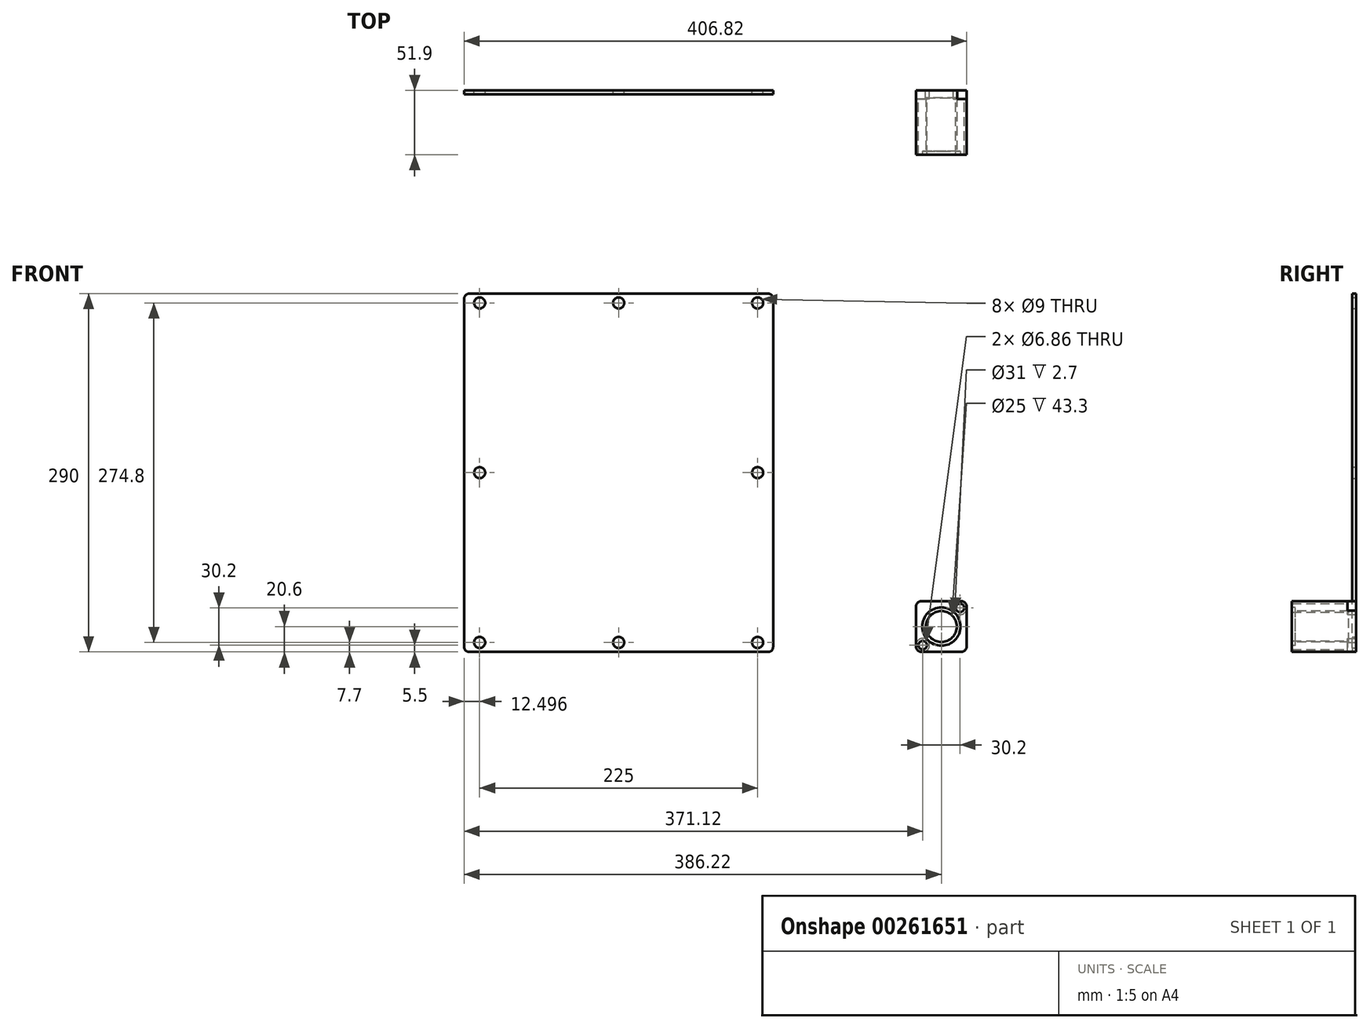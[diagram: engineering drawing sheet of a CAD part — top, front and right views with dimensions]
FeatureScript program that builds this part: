
annotation { "Feature Type Name" : "Feature", "Feature Type Description" : "" }
export const myFeature = defineFeature(function(context is Context, id is Id, definition is map)
    precondition{}
    {
        {
            var Q0;
            Q0=qCreatedBy(makeId("Front.planeOp"),FACE);
            var sketch = newSketch(context, id + "F0", { "sketchPlane" : qUnion([Q0])});
            skLineSegment(sketch, "E0.bottom", {"start": v(0, 0) * mm, "end": v(41.2, 0) * mm});
            skLineSegment(sketch, "E0.top", {"start": v(0, 41.2) * mm, "end": v(41.2, 41.2) * mm});
            skLineSegment(sketch, "E0.left", {"start": v(0, 0) * mm, "end": v(0, 41.2) * mm});
            skLineSegment(sketch, "E0.right", {"start": v(41.2, 0) * mm, "end": v(41.2, 41.2) * mm});
            skCircle(sketch, "E1", {"center": v(5.5, 5.5) * mm, "radius": 3.43 * mm});
            skCircle(sketch, "E2", {"center": v(35.7, 35.7) * mm, "radius": 3.43 * mm});
            skCircle(sketch, "E3", {"center": v(35.7, 35.7) * mm, "radius": 5.5 * mm});
            skCircle(sketch, "E4", {"center": v(5.5, 5.5) * mm, "radius": 5.5 * mm});
            skSolve(sketch);
        }
        {
            var Q0;
            {var subQ0=sQuery(id+"F0.wireOp",EDGE,"E0.left");var subQ1=sQuery(id+"F0.wireOp",EDGE,"E0.bottom");var subQ2=makeQuery(id+"F0.imprint","INTERSECT",VERTEX,{"derivedFrom":[subQ1,subQ0]});Q0=makeQuery(id+"F0.imprint","IMPRINT",FACE,{"disambiguationData":[TD([[makeQuery(id+"F0.imprint","IMPRINT",EDGE,{"disambiguationData":[TD([[subQ2,-1.0]])],"derivedFrom":subQ1}),1.0]])]});}
            var Q1;
            {var subQ0=sQuery(id+"F0.wireOp",EDGE,"E0.right");var subQ1=sQuery(id+"F0.wireOp",EDGE,"E0.top");var subQ2=makeQuery(id+"F0.imprint","INTERSECT",VERTEX,{"derivedFrom":[subQ1,subQ0]});Q1=makeQuery(id+"F0.imprint","IMPRINT",FACE,{"disambiguationData":[TD([[makeQuery(id+"F0.imprint","IMPRINT",EDGE,{"disambiguationData":[TD([[subQ2,1.0]])],"derivedFrom":subQ1}),-1.0]])]});}
            var Q2;
            Q2=makeQuery(id+"F0.imprint","IMPRINT",FACE,{"disambiguationData":[TD([[makeQuery(id+"F0.imprint","IMPRINT",EDGE,{"derivedFrom":sQuery(id+"F0.wireOp",EDGE,"E1")}),-1.0]])]});
            var Q3;
            Q3=makeQuery(id+"F0.imprint","IMPRINT",FACE,{"disambiguationData":[TD([[makeQuery(id+"F0.imprint","IMPRINT",EDGE,{"derivedFrom":sQuery(id+"F0.wireOp",EDGE,"E2")}),-1.0]])]});
            var Q4;
            {var subQ0=sQuery(id+"F0.wireOp",EDGE,"E0.right");var subQ1=sQuery(id+"F0.wireOp",EDGE,"E0.bottom");var subQ2=makeQuery(id+"F0.imprint","INTERSECT",VERTEX,{"derivedFrom":[subQ1,subQ0]});Q4=makeQuery(id+"F0.imprint","IMPRINT",FACE,{"disambiguationData":[TD([[makeQuery(id+"F0.imprint","IMPRINT",EDGE,{"disambiguationData":[TD([[subQ2,1.0]])],"derivedFrom":subQ1}),1.0]])]});}
            extrude(context, id + "F1", {"entities" : qUnion([Q0, Q1, Q2, Q3, Q4]), "depth" : 51.9 * mm});
        }
        {
            var Q0;
            Q0=makeQuery(id+"F1.opExtrude","CAP_FACE",FACE,{"disambiguationData":[OSD([sQuery(id+"F0.wireOp",EDGE,"E0.bottom"),sQuery(id+"F0.wireOp",EDGE,"E0.top"),sQuery(id+"F0.wireOp",EDGE,"E0.left"),sQuery(id+"F0.wireOp",EDGE,"E0.right"),sQuery(id+"F0.wireOp",EDGE,"E1"),sQuery(id+"F0.wireOp",EDGE,"E2")])],"isStart":true});
            var sketch = newSketch(context, id + "F2", { "sketchPlane" : qUnion([Q0])});
            skCircle(sketch, "E5", {"center": v(-35.7, 35.7) * mm, "radius": 5.5 * mm});
            skCircle(sketch, "E6", {"center": v(-5.5, 5.5) * mm, "radius": 5.5 * mm});
            skLineSegment(sketch, "E7", {"start": v(7.84, 0) * mm, "end": v(0, -7.71) * mm});
            skLineSegment(sketch, "E8", {"start": v(-39.53, 31.76) * mm, "end": v(-49.04, 41) * mm});
            skLineSegment(sketch, "E9", {"start": v(-49.04, 41) * mm, "end": v(-41.2, 48.71) * mm});
            skLineSegment(sketch, "E10", {"start": v(-41.2, 48.71) * mm, "end": v(-31.87, 39.64) * mm});
            skLineSegment(sketch, "E11", {"start": v(7.84, 0) * mm, "end": v(-1.62, 9.4) * mm});
            skLineSegment(sketch, "E12", {"start": v(0, -7.71) * mm, "end": v(-9.38, 1.6) * mm});
            skSolve(sketch);
        }
        {
            var Q0;
            Q0=makeQuery(id+"F2.imprint","IMPRINT",FACE,{"disambiguationData":[TD([[makeQuery(id+"F2.imprint","IMPRINT",EDGE,{"derivedFrom":makeQuery(id+"F1.opExtrude","CAP_EDGE",EDGE,{"disambiguationData":[OSD([sQuery(id+"F0.wireOp",EDGE,"E1")])],"isStart":true})}),1.0]])]});
            var Q1;
            {var subQ0=sQuery(id+"F2.wireOp",EDGE,"E5");var subQ1=makeQuery(id+"F1.opExtrude","CAP_EDGE",EDGE,{"disambiguationData":[OSD([sQuery(id+"F0.wireOp",EDGE,"E0.top")])],"isStart":true});var subQ2=makeQuery(id+"F2.imprint","INTERSECT",VERTEX,{"derivedFrom":[subQ1,subQ0]});Q1=makeQuery(id+"F2.imprint","IMPRINT",FACE,{"disambiguationData":[TD([[makeQuery(id+"F2.imprint","IMPRINT",EDGE,{"disambiguationData":[TD([[subQ2,-1.0]])],"derivedFrom":subQ0}),-1.0]])]});}
            var Q2;
            Q2=makeQuery(id+"F2.imprint","IMPRINT",FACE,{"disambiguationData":[TD([[makeQuery(id+"F2.imprint","IMPRINT",EDGE,{"derivedFrom":makeQuery(id+"F1.opExtrude","CAP_EDGE",EDGE,{"disambiguationData":[OSD([sQuery(id+"F0.wireOp",EDGE,"E2")])],"isStart":true})}),1.0]])]});
            var Q3;
            {var subQ0=sQuery(id+"F2.wireOp",EDGE,"E6");var subQ1=makeQuery(id+"F1.opExtrude","CAP_EDGE",EDGE,{"disambiguationData":[OSD([sQuery(id+"F0.wireOp",EDGE,"E0.left")])],"isStart":true});var subQ2=makeQuery(id+"F2.imprint","INTERSECT",VERTEX,{"derivedFrom":[subQ1,subQ0]});Q3=makeQuery(id+"F2.imprint","IMPRINT",FACE,{"disambiguationData":[TD([[makeQuery(id+"F2.imprint","IMPRINT",EDGE,{"disambiguationData":[TD([[subQ2,1.0]])],"derivedFrom":subQ0}),-1.0]])]});}
            var Q4;
            {var subQ0=sQuery(id+"F2.wireOp",EDGE,"E11");var subQ1=sQuery(id+"F2.wireOp",EDGE,"E6");var subQ2=makeQuery(id+"F2.imprint","INTERSECT",VERTEX,{"derivedFrom":[subQ1,subQ0]});Q4=makeQuery(id+"F2.imprint","IMPRINT",FACE,{"disambiguationData":[TD([[makeQuery(id+"F2.imprint","IMPRINT",EDGE,{"disambiguationData":[TD([[subQ2,1.0]])],"derivedFrom":subQ1}),-1.0]])]});}
            var Q5;
            {var subQ0=sQuery(id+"F2.wireOp",EDGE,"E12");var subQ1=sQuery(id+"F2.wireOp",EDGE,"E6");var subQ2=makeQuery(id+"F2.imprint","INTERSECT",VERTEX,{"derivedFrom":[subQ1,subQ0]});Q5=makeQuery(id+"F2.imprint","IMPRINT",FACE,{"disambiguationData":[TD([[makeQuery(id+"F2.imprint","IMPRINT",EDGE,{"disambiguationData":[TD([[subQ2,-1.0]])],"derivedFrom":subQ1}),-1.0]])]});}
            var Q6;
            {var subQ0=sQuery(id+"F2.wireOp",EDGE,"E10");var subQ1=sQuery(id+"F2.wireOp",EDGE,"E5");var subQ2=makeQuery(id+"F2.imprint","INTERSECT",VERTEX,{"derivedFrom":[subQ1,subQ0]});Q6=makeQuery(id+"F2.imprint","IMPRINT",FACE,{"disambiguationData":[TD([[makeQuery(id+"F2.imprint","IMPRINT",EDGE,{"disambiguationData":[TD([[subQ2,-1.0]])],"derivedFrom":subQ1}),-1.0]])]});}
            var Q7;
            {var subQ0=sQuery(id+"F2.wireOp",EDGE,"E8");var subQ1=sQuery(id+"F2.wireOp",EDGE,"E5");var subQ2=makeQuery(id+"F2.imprint","INTERSECT",VERTEX,{"derivedFrom":[subQ1,subQ0]});Q7=makeQuery(id+"F2.imprint","IMPRINT",FACE,{"disambiguationData":[TD([[makeQuery(id+"F2.imprint","IMPRINT",EDGE,{"disambiguationData":[TD([[subQ2,1.0]])],"derivedFrom":subQ1}),-1.0]])]});}
            extrude(context, id + "F3", {"entities" : qUnion([Q0, Q1, Q2, Q3, Q4, Q5, Q6, Q7]), "operationType" : NewBodyOperationType.REMOVE, "oppositeDirection" : true, "depth" : 7 * mm});
        }
        {
            var Q0;
            Q0=makeQuery(id+"F1.opExtrude","CAP_FACE",FACE,{"disambiguationData":[OSD([sQuery(id+"F0.wireOp",EDGE,"E0.bottom"),sQuery(id+"F0.wireOp",EDGE,"E0.top"),sQuery(id+"F0.wireOp",EDGE,"E0.left"),sQuery(id+"F0.wireOp",EDGE,"E0.right"),sQuery(id+"F0.wireOp",EDGE,"E1"),sQuery(id+"F0.wireOp",EDGE,"E2")])],"isStart":false});
            var sketch = newSketch(context, id + "F4", { "sketchPlane" : qUnion([Q0])});
            skCircle(sketch, "E13", {"center": v(20.6, 20.6) * mm, "radius": 12.5 * mm});
            skPoint(sketch, "E13.centerSnap0", {"position": v(0, 20.6) * mm});
            skPoint(sketch, "E13.centerSnap1", {"position": v(20.6, 41.2) * mm});
            skSolve(sketch);
        }
        {
            var Q0;
            Q0=makeQuery(id+"F4.imprint","IMPRINT",FACE,{"disambiguationData":[TD([[makeQuery(id+"F4.imprint","IMPRINT",EDGE,{"derivedFrom":sQuery(id+"F4.wireOp",EDGE,"E13")}),1.0]])]});
            extrude(context, id + "F5", {"entities" : qUnion([Q0]), "operationType" : NewBodyOperationType.REMOVE, "oppositeDirection" : true, "depth" : 46 * mm});
        }
        {
            var Q0;
            Q0=makeQuery(id+"F1.opExtrude","SWEPT_EDGE",EDGE,{"disambiguationData":[OSD([sQuery(id+"F0.wireOp",EDGE,"E0.bottom"),sQuery(id+"F0.wireOp",EDGE,"E0.right")])]});
            var Q1;
            Q1=makeQuery(id+"F1.opExtrude","SWEPT_EDGE",EDGE,{"disambiguationData":[OSD([sQuery(id+"F0.wireOp",EDGE,"E0.top"),sQuery(id+"F0.wireOp",EDGE,"E0.left")])]});
            var Q2;
            Q2=makeQuery(id+"F1.opExtrude","SWEPT_EDGE",EDGE,{"disambiguationData":[OSD([sQuery(id+"F0.wireOp",EDGE,"E0.top"),sQuery(id+"F0.wireOp",EDGE,"E0.right")])]});
            var Q3;
            Q3=makeQuery(id+"F1.opExtrude","SWEPT_EDGE",EDGE,{"disambiguationData":[OSD([sQuery(id+"F0.wireOp",EDGE,"E0.bottom"),sQuery(id+"F0.wireOp",EDGE,"E0.left")])]});
            fillet(context, id + "F6", {"entities" : qUnion([Q0, Q1, Q2, Q3]), "radius" : 5 * mm, "tangentPropagation" : true, "allowEdgeOverflow" : false});
        }
        {
            var Q0;
            Q0=makeQuery(id+"F1.opExtrude","CAP_FACE",FACE,{"disambiguationData":[OSD([sQuery(id+"F0.wireOp",EDGE,"E0.bottom"),sQuery(id+"F0.wireOp",EDGE,"E0.top"),sQuery(id+"F0.wireOp",EDGE,"E0.left"),sQuery(id+"F0.wireOp",EDGE,"E0.right"),sQuery(id+"F0.wireOp",EDGE,"E1"),sQuery(id+"F0.wireOp",EDGE,"E2")])],"isStart":false});
            var sketch = newSketch(context, id + "F7", { "sketchPlane" : qUnion([Q0])});
            skCircle(sketch, "E14", {"center": v(20.6, 20.6) * mm, "radius": 15.5 * mm});
            skSolve(sketch);
        }
        {
            var Q0;
            Q0=makeQuery(id+"F7.imprint","IMPRINT",FACE,{"disambiguationData":[TD([[makeQuery(id+"F7.imprint","IMPRINT",EDGE,{"derivedFrom":sQuery(id+"F7.wireOp",EDGE,"E14")}),1.0]])]});
            extrude(context, id + "F8", {"entities" : qUnion([Q0]), "operationType" : NewBodyOperationType.REMOVE, "oppositeDirection" : true, "depth" : 2.7 * mm});
        }
        {
            var Q0;
            Q0=qCreatedBy(makeId("Front.planeOp"),FACE);
            var sketch = newSketch(context, id + "F9", { "sketchPlane" : qUnion([Q0])});
            skLineSegment(sketch, "E15.bottom", {"start": v(-361.62, 0) * mm, "end": v(-119.62, 0) * mm});
            skLineSegment(sketch, "E15.top", {"start": v(-361.62, 290) * mm, "end": v(-119.62, 290) * mm});
            skLineSegment(sketch, "E15.left", {"start": v(-365.62, 4) * mm, "end": v(-365.62, 286) * mm});
            skLineSegment(sketch, "E15.right", {"start": v(-115.62, 4) * mm, "end": v(-115.62, 286) * mm});
            skLineSegment(sketch, "E16", {"start": v(-240.62, 341.05) * mm, "end": v(-240.62, -50.85) * mm, "construction": true});
            skPoint(sketch, "E16.startSnap0", {"position": v(-240.62, 290) * mm});
            skCircle(sketch, "E17", {"center": v(-240.62, 282.5) * mm, "radius": 4.5 * mm});
            skCircle(sketch, "E18", {"center": v(-128.12, 282.5) * mm, "radius": 4.5 * mm});
            skCircle(sketch, "E19", {"center": v(-353.12, 282.5) * mm, "radius": 4.5 * mm});
            skCircle(sketch, "E20", {"center": v(-353.12, 145.1) * mm, "radius": 4.5 * mm});
            skPoint(sketch, "E20.centerSnap0", {"position": v(-240.62, 145.1) * mm});
            skCircle(sketch, "E21", {"center": v(-128.12, 145.1) * mm, "radius": 4.5 * mm});
            skCircle(sketch, "E22", {"center": v(-128.12, 7.7) * mm, "radius": 4.5 * mm});
            skCircle(sketch, "E23", {"center": v(-353.12, 7.7) * mm, "radius": 4.5 * mm});
            skCircle(sketch, "E24", {"center": v(-240.62, 7.7) * mm, "radius": 4.5 * mm});
            skPoint(sketch, "E25.visualSharp", {"position": v(-365.62, 290) * mm});
            skArc(sketch, "E25.filletArc", {"start": v(-361.62, 290) * mm, "mid": v(-364.45, 288.83) * mm, "end": v(-365.62, 286) * mm});
            skPoint(sketch, "E26.visualSharp", {"position": v(-115.62, 290) * mm});
            skArc(sketch, "E26.filletArc", {"start": v(-115.62, 286) * mm, "mid": v(-116.8, 288.83) * mm, "end": v(-119.62, 290) * mm});
            skPoint(sketch, "E27.visualSharp", {"position": v(-115.62, 0) * mm});
            skArc(sketch, "E27.filletArc", {"start": v(-119.62, 0) * mm, "mid": v(-116.8, 1.17) * mm, "end": v(-115.62, 4) * mm});
            skPoint(sketch, "E28.visualSharp", {"position": v(-365.62, 0) * mm});
            skArc(sketch, "E28.filletArc", {"start": v(-365.62, 4) * mm, "mid": v(-364.45, 1.17) * mm, "end": v(-361.62, 0) * mm});
            skSolve(sketch);
        }
        {
            var Q0;
            Q0=makeQuery(id+"F9.imprint","IMPRINT",FACE,{"disambiguationData":[TD([[makeQuery(id+"F9.imprint","IMPRINT",EDGE,{"derivedFrom":sQuery(id+"F9.wireOp",EDGE,"E15.bottom")}),1.0]])]});
            extrude(context, id + "F10", {"entities" : qUnion([Q0]), "depth" : 3 * mm});
        }
    });
